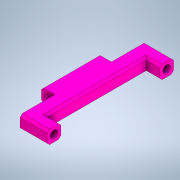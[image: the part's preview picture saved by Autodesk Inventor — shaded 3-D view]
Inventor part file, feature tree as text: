
AUTODESK INVENTOR PART (.ipt)
format: ipt  version: 2020 (Build 240168000, 168)  size: 156,672 bytes
history: native  units: mm
features: extrude x3, sketch x3, chamfer x1
ambient origin geometry x8: Origin, YZ Plane, XZ Plane, XY Plane, X Axis, Y Axis, Z Axis, Center Point
bodies: Solid1 (feature_tree)
feature tree (7):
  extrude  "Extrusion1"  Depth=6.0mm
  extrude  "Extrusion2"  Depth=6.0mm
  extrude  "Extrusion3"  Depth=12.0mm
  chamfer  "Chamfer1"  Distance=6.0mm
  sketch  "Sketch1"  dims[d0=25.0mm d1=6.0mm]
  sketch  "Sketch2"  dims[d2=50.0mm d3=6.0mm]
  sketch  "Sketch3"  dims[d4=6.0mm d5=12.0mm d6=6.0mm d7=0.0mm d8=3.4mm d9=0.0mm d10=0.0mm d11=3.4mm d12=0.0mm d13=0.0mm d14=1.0mm d15=2.0mm d16=45.0deg]
